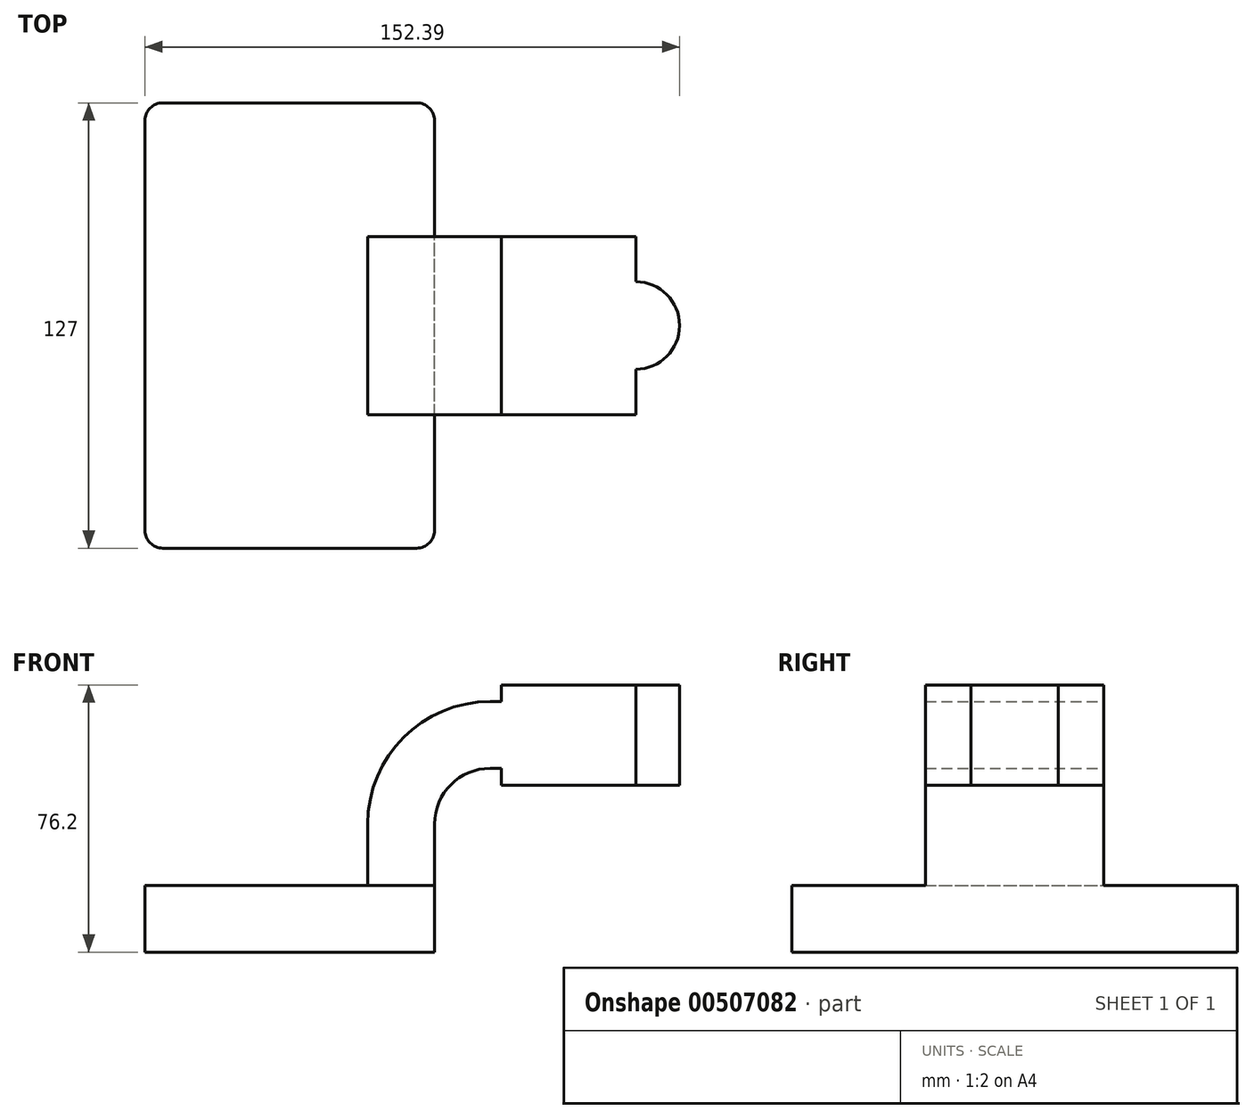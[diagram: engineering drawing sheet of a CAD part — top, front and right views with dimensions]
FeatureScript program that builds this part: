
annotation { "Feature Type Name" : "Feature", "Feature Type Description" : "" }
export const myFeature = defineFeature(function(context is Context, id is Id, definition is map)
    precondition{}
    {
        {
            var Q0;
            Q0=qCreatedBy(makeId("Front.planeOp"),FACE);
            var sketch = newSketch(context, id + "F0", { "sketchPlane" : qUnion([Q0])});
            skLineSegment(sketch, "E0.bottom", {"start": v(-41.27, 9.52) * mm, "end": v(41.28, 9.52) * mm});
            skLineSegment(sketch, "E0.top", {"start": v(-41.28, -9.53) * mm, "end": v(41.27, -9.53) * mm});
            skLineSegment(sketch, "E0.left", {"start": v(-41.28, 9.52) * mm, "end": v(-41.28, -9.53) * mm});
            skLineSegment(sketch, "E0.right", {"start": v(41.28, 9.52) * mm, "end": v(41.27, -9.53) * mm});
            skPoint(sketch, "E0.middle", {"position": v(0, 0) * mm});
            skLineSegment(sketch, "E1.bottom", {"start": v(111.12, 66.68) * mm, "end": v(60.32, 66.68) * mm});
            skLineSegment(sketch, "E1.top", {"start": v(111.12, 38.1) * mm, "end": v(60.32, 38.1) * mm});
            skLineSegment(sketch, "E1.left", {"start": v(111.12, 66.68) * mm, "end": v(111.12, 38.1) * mm});
            skLineSegment(sketch, "E1.right", {"start": v(60.32, 66.67) * mm, "end": v(60.32, 38.1) * mm});
            skPoint(sketch, "E1.middle", {"position": v(85.72, 52.39) * mm});
            skLineSegment(sketch, "E2", {"start": v(41.28, 9.52) * mm, "end": v(41.28, 27) * mm});
            skArc(sketch, "E3", {"start": v(41.27, 27) * mm, "mid": v(45.92, 38.23) * mm, "end": v(57.15, 42.88) * mm});
            skLineSegment(sketch, "E4", {"start": v(57.15, 42.88) * mm, "end": v(98.65, 42.88) * mm});
            skLineSegment(sketch, "E5.0", {"start": v(57.15, 61.93) * mm, "end": v(98.65, 61.93) * mm});
            skArc(sketch, "E5.1", {"start": v(22.23, 27) * mm, "mid": v(32.45, 51.7) * mm, "end": v(57.15, 61.93) * mm});
            skLineSegment(sketch, "E5.2", {"start": v(22.22, 9.52) * mm, "end": v(22.22, 27) * mm});
            skLineSegment(sketch, "E6", {"start": v(98.65, 38.1) * mm, "end": v(98.65, 66.68) * mm});
            skPoint(sketch, "E6.startSnap0", {"position": v(85.72, 38.1) * mm});
            skFitSpline(sketch, "E7", {"points": [v(-41.28, 9.53) * mm, v(60.32, 61.93) * mm], "startDerivative": vector(25.92, 126.9) * mm, "endDerivative": vector(122.93, -17.98) * mm});
            skSolve(sketch);
        }
        {
            var Q0;
            Q0=makeQuery(id+"F0.imprint","IMPRINT",FACE,{"disambiguationData":[TD([[makeQuery(id+"F0.imprint","IMPRINT",EDGE,{"derivedFrom":sQuery(id+"F0.wireOp",EDGE,"E0.top")}),1.0]])]});
            extrude(context, id + "F1", {"entities" : qUnion([Q0]), "endBound" : BoundingType.SYMMETRIC, "depth" : 127 * mm});
        }
        {
            var Q0;
            Q0=makeQuery(id+"F0.imprint","IMPRINT",FACE,{"disambiguationData":[TD([[makeQuery(id+"F0.imprint","IMPRINT",EDGE,{"derivedFrom":sQuery(id+"F0.wireOp",EDGE,"E0.top")}),1.0]])]});
            var Q1;
            {var subQ0=sQuery(id+"F0.wireOp",EDGE,"E1.right");var subQ1=sQuery(id+"F0.wireOp",EDGE,"E1.bottom");var subQ2=makeQuery(id+"F0.imprint","INTERSECT",VERTEX,{"derivedFrom":[subQ1,subQ0]});Q1=makeQuery(id+"F0.imprint","IMPRINT",FACE,{"disambiguationData":[TD([[makeQuery(id+"F0.imprint","IMPRINT",EDGE,{"disambiguationData":[TD([[subQ2,1.0]])],"derivedFrom":subQ1}),1.0]])]});}
            var Q2;
            {var subQ0=sQuery(id+"F0.wireOp",EDGE,"E1.right");var subQ1=sQuery(id+"F0.wireOp",EDGE,"E1.top");var subQ2=makeQuery(id+"F0.imprint","INTERSECT",VERTEX,{"derivedFrom":[subQ1,subQ0]});Q2=makeQuery(id+"F0.imprint","IMPRINT",FACE,{"disambiguationData":[TD([[makeQuery(id+"F0.imprint","IMPRINT",EDGE,{"disambiguationData":[TD([[subQ2,1.0]])],"derivedFrom":subQ1}),-1.0]])]});}
            var Q3;
            {var subQ1=sQuery(id+"F0.wireOp",EDGE,"E2");Q3=makeQuery(id+"F0.imprint","IMPRINT",FACE,{"disambiguationData":[TD([[makeQuery(id+"F0.imprint","IMPRINT",EDGE,{"derivedFrom":subQ1}),1.0]])]});}
            var Q4;
            {var subQ3=sQuery(id+"F0.wireOp",EDGE,"E4");var subQ5=sQuery(id+"F0.wireOp",EDGE,"E6");var subQ6=makeQuery(id+"F0.imprint","INTERSECT",VERTEX,{"derivedFrom":[subQ3,subQ5]});Q4=makeQuery(id+"F0.imprint","IMPRINT",FACE,{"disambiguationData":[TD([[makeQuery(id+"F0.imprint","IMPRINT",EDGE,{"disambiguationData":[TD([[subQ6,1.0]])],"derivedFrom":subQ3}),1.0]])]});}
            extrude(context, id + "F2", {"entities" : qUnion([Q0, Q1, Q2, Q3, Q4]), "operationType" : NewBodyOperationType.ADD, "endBound" : BoundingType.SYMMETRIC, "depth" : 50.8 * mm});
        }
        {
            var Q0;
            {var subQ0=sQuery(id+"F0.wireOp",EDGE,"E5.1");Q0=makeQuery(id+"F0.imprint","IMPRINT",FACE,{"disambiguationData":[TD([[makeQuery(id+"F0.imprint","IMPRINT",EDGE,{"derivedFrom":subQ0}),1.0]])]});}
            extrude(context, id + "F3", {"entities" : qUnion([Q0]), "operationType" : NewBodyOperationType.ADD, "endBound" : BoundingType.SYMMETRIC, "depth" : 15.88 * mm});
        }
        {
            var Q0;
            {var subQ4=sQuery(id+"F0.wireOp",EDGE,"E1.left");Q0=makeQuery(id+"F0.imprint","IMPRINT",FACE,{"disambiguationData":[TD([[makeQuery(id+"F0.imprint","IMPRINT",EDGE,{"derivedFrom":subQ4}),-1.0]])]});}
            var Q1;
            Q1=sQuery(id+"F0.wireOp",EDGE,"E6");
            revolve(context, id + "F4", {"operationType" : NewBodyOperationType.ADD, "entities" : qUnion([Q0]), "axis" : qUnion([Q1]), "revolveType" : RevolveType.FULL});
        }
        {
            var Q0;
            Q0=makeQuery(id+"F1.opExtrude","CAP_EDGE",EDGE,{"disambiguationData":[OSD([sQuery(id+"F0.wireOp",EDGE,"E0.left")])],"isStart":false});
            var Q1;
            Q1=makeQuery(id+"F1.opExtrude","CAP_EDGE",EDGE,{"disambiguationData":[OSD([sQuery(id+"F0.wireOp",EDGE,"E0.right")])],"isStart":false});
            var Q2;
            Q2=makeQuery(id+"F1.opExtrude","CAP_EDGE",EDGE,{"disambiguationData":[OSD([sQuery(id+"F0.wireOp",EDGE,"E0.right")])],"isStart":true});
            var Q3;
            Q3=makeQuery(id+"F1.opExtrude","CAP_EDGE",EDGE,{"disambiguationData":[OSD([sQuery(id+"F0.wireOp",EDGE,"E0.left")])],"isStart":true});
            fillet(context, id + "F5", {"entities" : qUnion([Q0, Q1, Q2, Q3]), "radius" : 5.08 * mm, "tangentPropagation" : true, "allowEdgeOverflow" : false});
        }
    });
